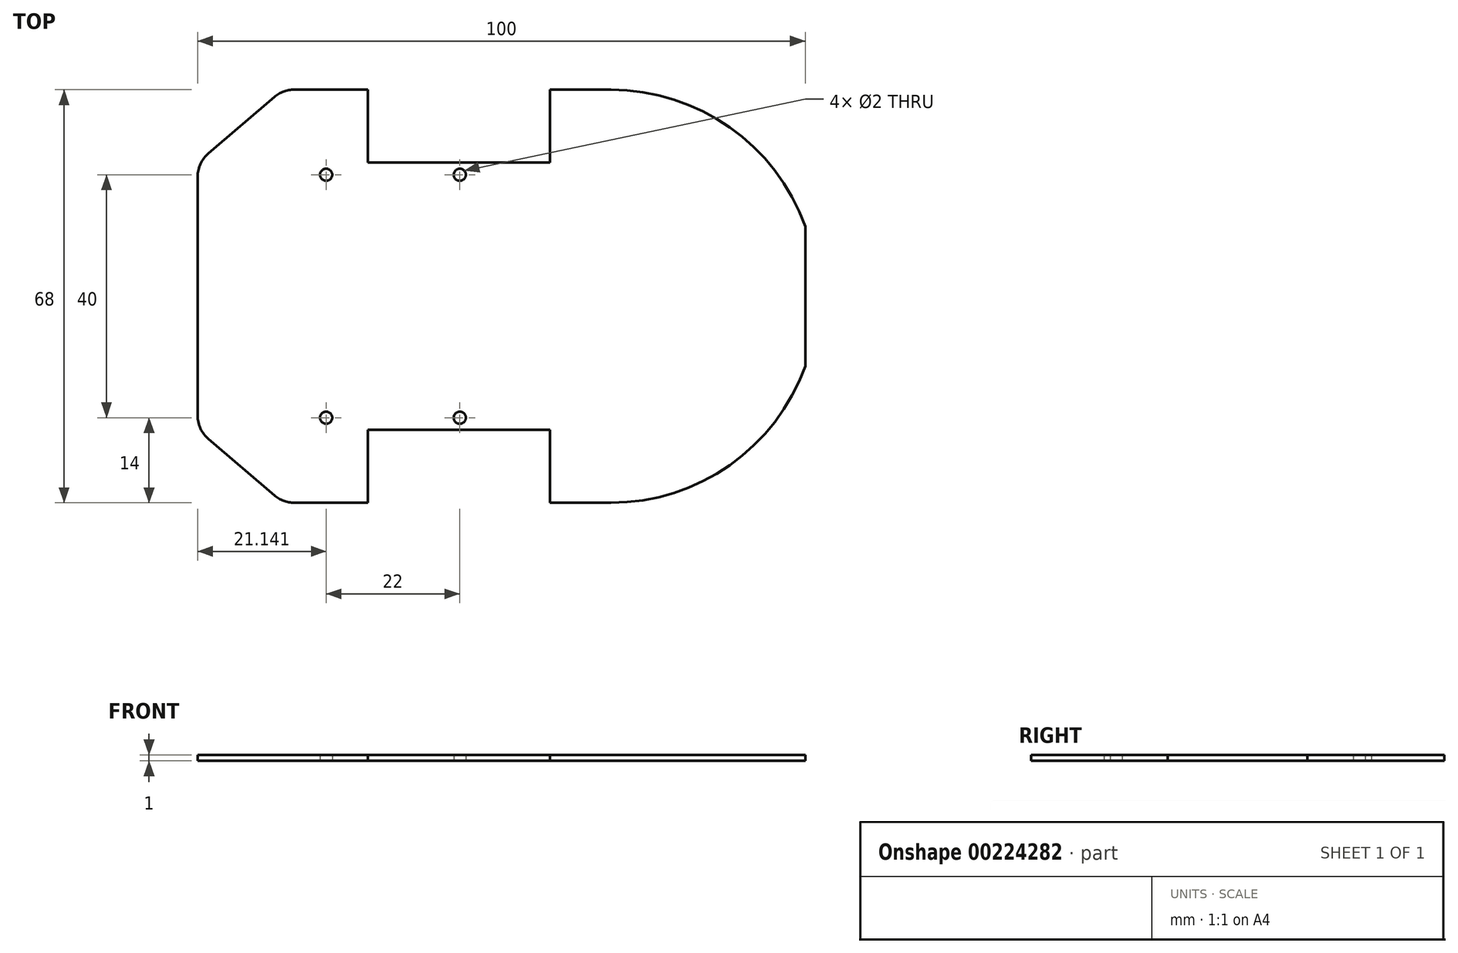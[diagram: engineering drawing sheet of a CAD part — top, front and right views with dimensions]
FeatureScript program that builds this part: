
annotation { "Feature Type Name" : "Feature", "Feature Type Description" : "" }
export const myFeature = defineFeature(function(context is Context, id is Id, definition is map)
    precondition{}
    {
        {
            var Q0;
            Q0=qCreatedBy(makeId("Top.planeOp"),FACE);
            var sketch = newSketch(context, id + "F0", { "sketchPlane" : qUnion([Q0])});
            skLineSegment(sketch, "E0", {"start": v(0, 0) * mm, "end": v(0, 22) * mm});
            skLineSegment(sketch, "E1", {"start": v(0, 22) * mm, "end": v(14.04, 34) * mm});
            skLineSegment(sketch, "E2.MirrorCS", {"start": v(0, 0) * mm, "end": v(0, -22) * mm});
            skLineSegment(sketch, "E3.MirrorCS", {"start": v(0, -22) * mm, "end": v(14.04, -34) * mm});
            skLineSegment(sketch, "E4", {"start": v(58, 22) * mm, "end": v(58, 34) * mm});
            skLineSegment(sketch, "E5", {"start": v(58, -22) * mm, "end": v(58, -34) * mm});
            skLineSegment(sketch, "E6", {"start": v(58, 34) * mm, "end": v(68, 34) * mm});
            skLineSegment(sketch, "E7", {"start": v(58, -34) * mm, "end": v(68, -34) * mm});
            skArc(sketch, "E8", {"start": v(68, -34) * mm, "mid": v(87.56, -27.8) * mm, "end": v(100, -11.49) * mm});
            skLineSegment(sketch, "E9", {"start": v(58, 22) * mm, "end": v(28, 22) * mm});
            skLineSegment(sketch, "E10", {"start": v(28, 22) * mm, "end": v(28, 34) * mm});
            skLineSegment(sketch, "E11", {"start": v(28, 34) * mm, "end": v(14.04, 34) * mm});
            skLineSegment(sketch, "E12.MirrorCS", {"start": v(58, -22) * mm, "end": v(28, -22) * mm});
            skLineSegment(sketch, "E13.MirrorCS", {"start": v(28, -22) * mm, "end": v(28, -34) * mm});
            skLineSegment(sketch, "E14.MirrorCS", {"start": v(28, -34) * mm, "end": v(14.04, -34) * mm});
            skPoint(sketch, "E15", {"position": v(28, 22) * mm});
            skPoint(sketch, "E16", {"position": v(21.14, 20) * mm});
            skCircle(sketch, "E17", {"center": v(21.14, 20) * mm, "radius": 1 * mm});
            skPoint(sketch, "E18", {"position": v(43.14, 20) * mm});
            skCircle(sketch, "E19", {"center": v(43.14, 20) * mm, "radius": 1 * mm});
            skCircle(sketch, "E20.MirrorC", {"center": v(21.14, -20) * mm, "radius": 1 * mm});
            skCircle(sketch, "E21.MirrorC", {"center": v(43.14, -20) * mm, "radius": 1 * mm});
            skLineSegment(sketch, "E22", {"start": v(100, 11.49) * mm, "end": v(100, -11.49) * mm});
            skArc(sketch, "E23.trimOffspring", {"start": v(100, 11.49) * mm, "mid": v(87.56, 27.8) * mm, "end": v(68, 34) * mm});
            skSolve(sketch);
        }
        {
            var Q0;
            Q0 = qSketchRegion(id + "F0", true);
            extrude(context, id + "F1", {"entities" : qUnion([Q0]), "depth" : 1 * mm});
        }
        {
            var Q0;
            Q0=makeQuery(id+"F1.opExtrude","SWEPT_EDGE",EDGE,{"disambiguationData":[OSD([sQuery(id+"F0.wireOp",EDGE,"E1"),sQuery(id+"F0.wireOp",EDGE,"E11")])]});
            fillet(context, id + "F2", {"entities" : qUnion([Q0]), "radius" : 5.08 * mm, "tangentPropagation" : true, "allowEdgeOverflow" : false});
        }
        {
            var Q0;
            Q0=makeQuery(id+"F1.opExtrude","SWEPT_EDGE",EDGE,{"disambiguationData":[OSD([sQuery(id+"F0.wireOp",EDGE,"E0"),sQuery(id+"F0.wireOp",EDGE,"E1")])]});
            fillet(context, id + "F3", {"entities" : qUnion([Q0]), "radius" : 5.08 * mm, "tangentPropagation" : true, "allowEdgeOverflow" : false});
        }
        {
            var Q0;
            Q0=makeQuery(id+"F1.opExtrude","SWEPT_EDGE",EDGE,{"disambiguationData":[OSD([sQuery(id+"F0.wireOp",EDGE,"E2.MirrorCS"),sQuery(id+"F0.wireOp",EDGE,"E3.MirrorCS")])]});
            fillet(context, id + "F4", {"entities" : qUnion([Q0]), "radius" : 5.08 * mm, "tangentPropagation" : true, "allowEdgeOverflow" : false});
        }
        {
            var Q0;
            Q0=makeQuery(id+"F1.opExtrude","SWEPT_EDGE",EDGE,{"disambiguationData":[OSD([sQuery(id+"F0.wireOp",EDGE,"E3.MirrorCS"),sQuery(id+"F0.wireOp",EDGE,"E14.MirrorCS")])]});
            fillet(context, id + "F5", {"entities" : qUnion([Q0]), "radius" : 5.08 * mm, "tangentPropagation" : true, "allowEdgeOverflow" : false});
        }
    });
